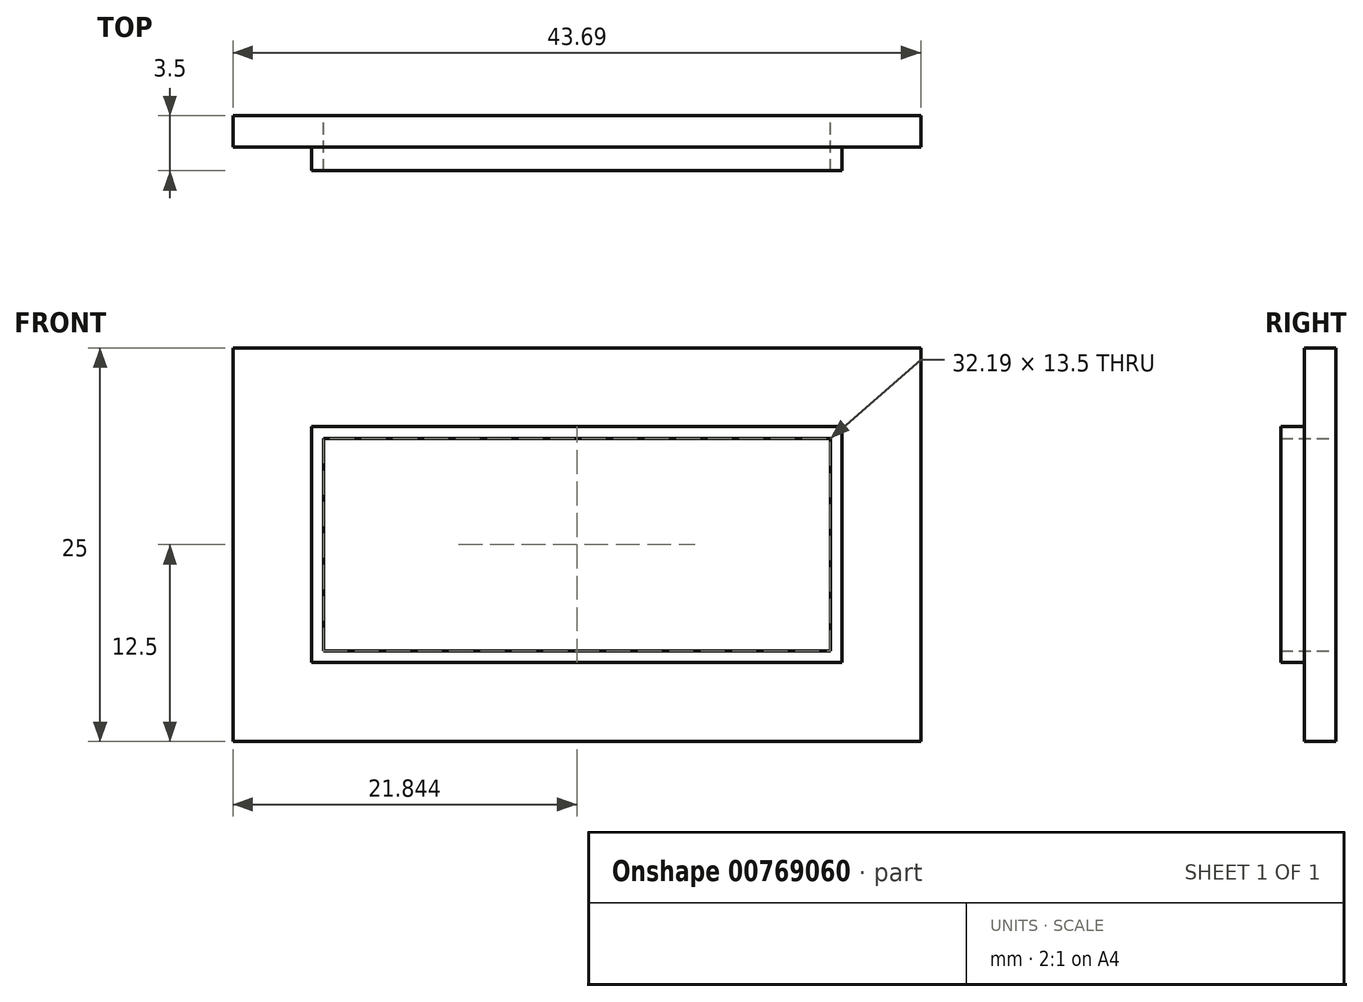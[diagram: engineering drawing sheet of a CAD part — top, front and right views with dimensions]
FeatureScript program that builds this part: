
annotation { "Feature Type Name" : "Feature", "Feature Type Description" : "" }
export const myFeature = defineFeature(function(context is Context, id is Id, definition is map)
    precondition{}
    {
        {
            var Q0;
            Q0=qCreatedBy(makeId("Front.planeOp"),FACE);
            var sketch = newSketch(context, id + "F0", { "sketchPlane" : qUnion([Q0])});
            skLineSegment(sketch, "E0.bottom", {"start": v(0, 0) * mm, "end": v(33.69, 0) * mm});
            skLineSegment(sketch, "E0.top", {"start": v(0, -15) * mm, "end": v(33.69, -15) * mm});
            skLineSegment(sketch, "E0.left", {"start": v(0, 0) * mm, "end": v(0, -15) * mm});
            skLineSegment(sketch, "E0.right", {"start": v(33.69, 0) * mm, "end": v(33.69, -15) * mm});
            skLineSegment(sketch, "E1.0", {"start": v(-5, 5) * mm, "end": v(38.69, 5) * mm});
            skLineSegment(sketch, "E1.1", {"start": v(-5, 5) * mm, "end": v(-5, -20) * mm});
            skLineSegment(sketch, "E1.2", {"start": v(-5, -20) * mm, "end": v(38.69, -20) * mm});
            skLineSegment(sketch, "E1.3", {"start": v(38.69, 5) * mm, "end": v(38.69, -20) * mm});
            skLineSegment(sketch, "E2.0", {"start": v(0.75, -0.75) * mm, "end": v(0.75, -14.25) * mm});
            skLineSegment(sketch, "E2.1", {"start": v(0.75, -0.75) * mm, "end": v(32.94, -0.75) * mm});
            skLineSegment(sketch, "E2.2", {"start": v(32.94, -0.75) * mm, "end": v(32.94, -14.25) * mm});
            skLineSegment(sketch, "E2.3", {"start": v(0.75, -14.25) * mm, "end": v(32.94, -14.25) * mm});
            skSolve(sketch);
        }
        {
            var Q0;
            Q0=makeQuery(id+"F0.imprint","IMPRINT",FACE,{"disambiguationData":[TD([[makeQuery(id+"F0.imprint","IMPRINT",EDGE,{"derivedFrom":sQuery(id+"F0.wireOp",EDGE,"E0.bottom")}),-1.0]])]});
            extrude(context, id + "F1", {"entities" : qUnion([Q0]), "depth" : 3.5 * mm, "offsetDistance" : 25 * mm});
        }
        {
            var Q0;
            Q0=makeQuery(id+"F0.imprint","IMPRINT",FACE,{"disambiguationData":[TD([[makeQuery(id+"F0.imprint","IMPRINT",EDGE,{"derivedFrom":sQuery(id+"F0.wireOp",EDGE,"E0.bottom")}),1.0]])]});
            extrude(context, id + "F2", {"entities" : qUnion([Q0]), "operationType" : NewBodyOperationType.ADD, "depth" : 2 * mm, "offsetDistance" : 25 * mm});
        }
    });
